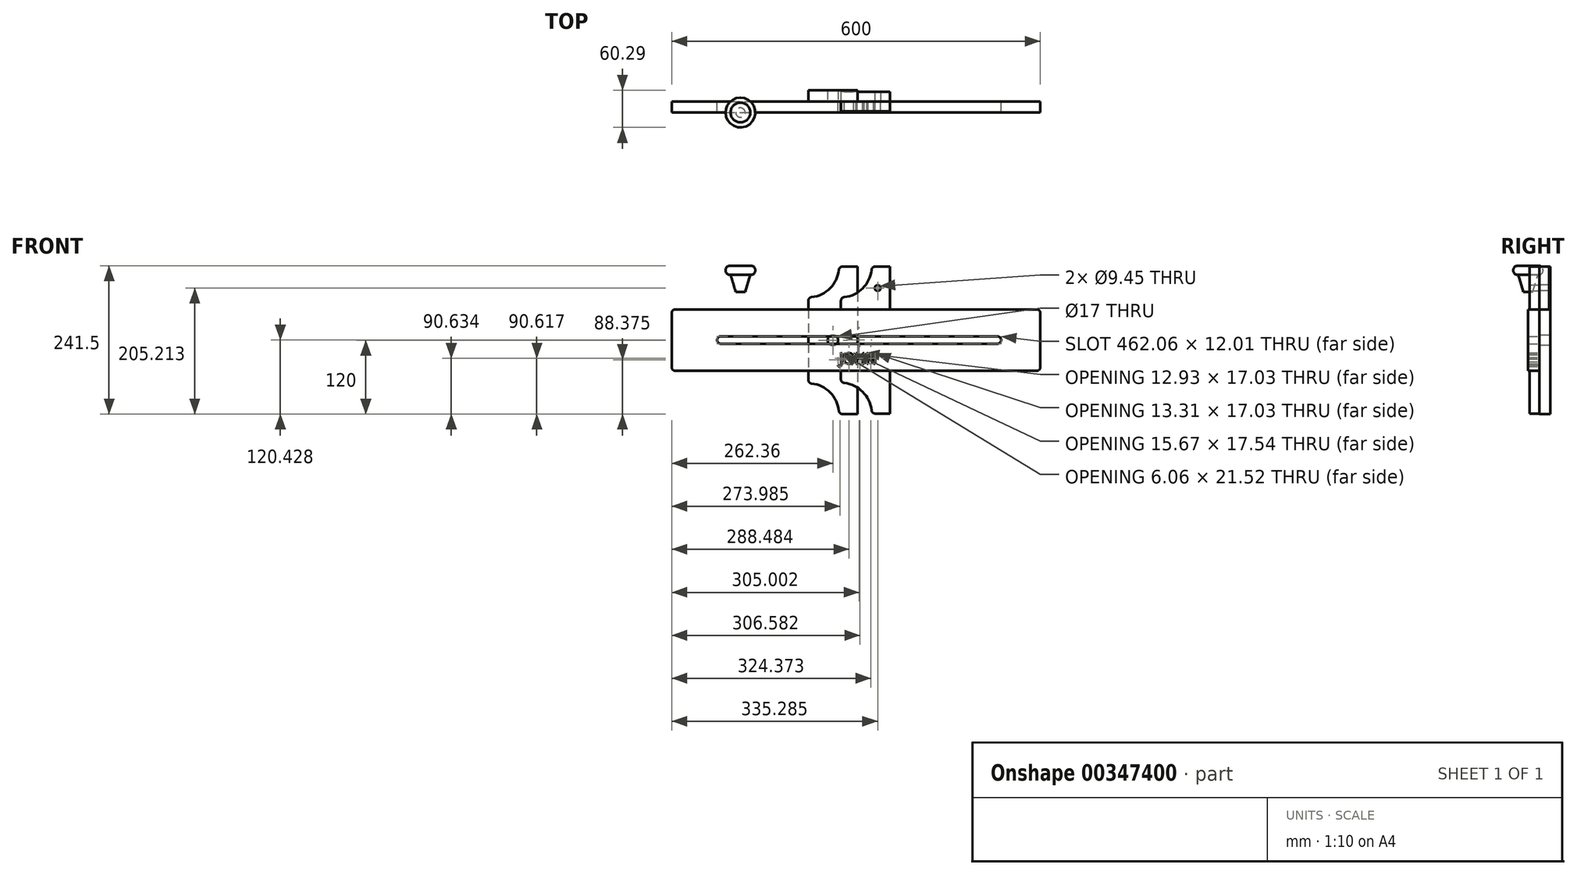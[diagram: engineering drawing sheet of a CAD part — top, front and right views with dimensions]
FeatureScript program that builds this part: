
annotation { "Feature Type Name" : "Feature", "Feature Type Description" : "" }
export const myFeature = defineFeature(function(context is Context, id is Id, definition is map)
    precondition{}
    {
        {
            var Q0;
            Q0=qCreatedBy(makeId("Front.planeOp"),FACE);
            var sketch = newSketch(context, id + "F0", { "sketchPlane" : qUnion([Q0])});
            skLineSegment(sketch, "E0.bottom", {"start": v(-296.36, 50.43) * mm, "end": v(291.64, 50.43) * mm});
            skLineSegment(sketch, "E0.top", {"start": v(-296.36, -49.57) * mm, "end": v(291.64, -49.57) * mm});
            skLineSegment(sketch, "E0.left", {"start": v(-302.36, 44.43) * mm, "end": v(-302.36, -43.57) * mm});
            skLineSegment(sketch, "E0.right", {"start": v(297.64, 44.43) * mm, "end": v(297.64, -43.57) * mm});
            skLineSegment(sketch, "E1", {"start": v(-302.36, 0.43) * mm, "end": v(297.64, 0.43) * mm});
            skCircle(sketch, "E2", {"center": v(-222.39, 0.43) * mm, "radius": 6 * mm});
            skCircle(sketch, "E3", {"center": v(227.67, 0.43) * mm, "radius": 6 * mm});
            skLineSegment(sketch, "E4", {"start": v(-222.39, -5.58) * mm, "end": v(227.67, -5.57) * mm});
            skLineSegment(sketch, "E5", {"start": v(227.67, 6.43) * mm, "end": v(-222.39, 6.43) * mm});
            skPoint(sketch, "E6.visualSharp", {"position": v(-302.36, 50.43) * mm});
            skArc(sketch, "E6.filletArc", {"start": v(-296.36, 50.43) * mm, "mid": v(-300.6, 48.67) * mm, "end": v(-302.36, 44.43) * mm});
            skPoint(sketch, "E7.visualSharp", {"position": v(-302.36, -49.57) * mm});
            skArc(sketch, "E7.filletArc", {"start": v(-302.36, -43.57) * mm, "mid": v(-300.6, -47.81) * mm, "end": v(-296.36, -49.57) * mm});
            skPoint(sketch, "E8.visualSharp", {"position": v(297.64, 50.43) * mm});
            skArc(sketch, "E8.filletArc", {"start": v(297.64, 44.43) * mm, "mid": v(295.88, 48.67) * mm, "end": v(291.64, 50.43) * mm});
            skPoint(sketch, "E9.visualSharp", {"position": v(297.64, -49.57) * mm});
            skArc(sketch, "E9.filletArc", {"start": v(291.64, -49.57) * mm, "mid": v(295.88, -47.81) * mm, "end": v(297.64, -43.57) * mm});
            skText(sketch, "E10", { "text": "JOHN", "fontName": "OpenSans-Regular.ttf"});
            const initialGuessF0  = {"E10": [-0.02954, -0.0379, 1, 0, 0.01718]};
            skSetInitialGuess(sketch, initialGuessF0);
            skSolve(sketch);
        }
        {
            var Q0;
            {var subQ6=sQuery(id+"F0.wireOp",EDGE,"E0.bottom");Q0=makeQuery(id+"F0.imprint","IMPRINT",FACE,{"disambiguationData":[TD([[makeQuery(id+"F0.imprint","IMPRINT",EDGE,{"derivedFrom":subQ6}),-1.0]])]});}
            var Q1;
            {var subQ1=sQuery(id+"F0.wireOp",EDGE,"E0.top");Q1=makeQuery(id+"F0.imprint","IMPRINT",FACE,{"disambiguationData":[TD([[makeQuery(id+"F0.imprint","IMPRINT",EDGE,{"derivedFrom":subQ1}),1.0]])]});}
            var Q2;
            Q2=sQuery(id+"F0.wireOp",EDGE,"E0.bottom");
            var Q3;
            Q3=sQuery(id+"F0.wireOp",EDGE,"E0.left");
            var Q4;
            Q4=sQuery(id+"F0.wireOp",EDGE,"E0.top");
            var Q5;
            Q5=sQuery(id+"F0.wireOp",EDGE,"E0.right");
            extrude(context, id + "F1", {"entities" : qUnion([Q0, Q1]), "surfaceEntities" : qUnion([Q2, Q3, Q4, Q5]), "depth" : 18 * mm});
        }
        {
            var Q0;
            Q0=qCreatedBy(makeId("Front.planeOp"),FACE);
            var sketch = newSketch(context, id + "F2", { "sketchPlane" : qUnion([Q0])});
            skLineSegment(sketch, "E11.left", {"start": v(0, 120) * mm, "end": v(0, 0) * mm});
            skPoint(sketch, "E12.visualSharp", {"position": v(-80, 120) * mm});
            skArc(sketch, "E13.MirrorCS", {"start": v(-30.29, 114.64) * mm, "mid": v(-44.64, 84.64) * mm, "end": v(-74.64, 70.29) * mm});
            skLineSegment(sketch, "E14", {"start": v(-24.32, 120) * mm, "end": v(0, 120) * mm});
            skLineSegment(sketch, "E15", {"start": v(-80, 64.32) * mm, "end": v(-80, 6) * mm});
            skPoint(sketch, "E16.visualSharp", {"position": v(-80, 0) * mm});
            skPoint(sketch, "E17.visualSharp", {"position": v(-80, 70) * mm});
            skArc(sketch, "E17.filletArc", {"start": v(-74.64, 70.29) * mm, "mid": v(-78.46, 68.33) * mm, "end": v(-80, 64.32) * mm});
            skPoint(sketch, "E18.visualSharp", {"position": v(-30, 120) * mm});
            skArc(sketch, "E18.filletArc", {"start": v(-24.32, 120) * mm, "mid": v(-28.33, 118.46) * mm, "end": v(-30.29, 114.64) * mm});
            skLineSegment(sketch, "E19", {"start": v(-80, 6) * mm, "end": v(-80, 0) * mm});
            skLineSegment(sketch, "E20.MirrorCS", {"start": v(0, -120) * mm, "end": v(0, 0) * mm});
            skArc(sketch, "E21.MirrorCS", {"start": v(-74.64, -70.29) * mm, "mid": v(-78.46, -68.33) * mm, "end": v(-80, -64.32) * mm});
            skArc(sketch, "E22.MirrorCS", {"start": v(-24.32, -120) * mm, "mid": v(-28.33, -118.46) * mm, "end": v(-30.29, -114.64) * mm});
            skPoint(sketch, "E23.MirrorP", {"position": v(-30, -120) * mm});
            skPoint(sketch, "E24.MirrorP", {"position": v(-80, -70) * mm});
            skPoint(sketch, "E25.MirrorP", {"position": v(-80, -120) * mm});
            skLineSegment(sketch, "E26.MirrorCS", {"start": v(-24.32, -120) * mm, "end": v(0, -120) * mm});
            skLineSegment(sketch, "E27.MirrorCS", {"start": v(-80, -64.32) * mm, "end": v(-80, -6) * mm});
            skPoint(sketch, "E28.MirrorP", {"position": v(-83.16, 0) * mm});
            skArc(sketch, "E29.MirrorCS", {"start": v(-30.29, -114.64) * mm, "mid": v(-44.64, -84.64) * mm, "end": v(-74.64, -70.29) * mm});
            skLineSegment(sketch, "E30", {"start": v(-80, -6) * mm, "end": v(-80, 0) * mm});
            skCircle(sketch, "E31", {"center": v(-40, 0) * mm, "radius": 8.5 * mm});
            skLineSegment(sketch, "E32", {"start": v(-80, 0) * mm, "end": v(0, 0) * mm});
            skSolve(sketch);
        }
        {
            var Q0;
            Q0 = qSketchRegion(id + "F2", true);
            extrude(context, id + "F3", {"entities" : qUnion([Q0]), "oppositeDirection" : true, "depth" : 18 * mm});
        }
        {
            var Q0;
            Q0=sQuery(id+"F2.wireOp",EDGE,"E31");
            extrude(context, id + "F4", {"bodyType" : ToolBodyType.SURFACE, "surfaceEntities" : qUnion([Q0]), "oppositeDirection" : true, "depth" : 18 * mm});
        }
        {
            var Q0;
            Q0=qCreatedBy(makeId("Front.planeOp"),FACE);
            var sketch = newSketch(context, id + "F5", { "sketchPlane" : qUnion([Q0])});
            skPoint(sketch, "E33.visualSharp", {"position": v(-26.9, 120) * mm});
            skArc(sketch, "E34.MirrorCS", {"start": v(22.8, 114.64) * mm, "mid": v(8.45, 84.64) * mm, "end": v(-21.55, 70.29) * mm});
            skLineSegment(sketch, "E35", {"start": v(28.77, 120) * mm, "end": v(53.1, 120) * mm});
            skPoint(sketch, "E36.visualSharp", {"position": v(-26.91, 0) * mm});
            skPoint(sketch, "E37.visualSharp", {"position": v(-26.9, 70) * mm});
            skArc(sketch, "E37.filletArc", {"start": v(-21.55, 70.29) * mm, "mid": v(-25.37, 68.33) * mm, "end": v(-26.9, 64.32) * mm});
            skPoint(sketch, "E38.visualSharp", {"position": v(23.1, 120) * mm});
            skArc(sketch, "E38.filletArc", {"start": v(28.77, 120) * mm, "mid": v(24.76, 118.46) * mm, "end": v(22.8, 114.64) * mm});
            skPoint(sketch, "E39.MirrorP", {"position": v(-26.9, -70) * mm});
            skPoint(sketch, "E40.MirrorP", {"position": v(-26.9, -120) * mm});
            skPoint(sketch, "E41.MirrorP", {"position": v(-30.07, 0) * mm});
            skLineSegment(sketch, "E42", {"start": v(53.15, 50.43) * mm, "end": v(-26.9, 50.43) * mm});
            skLineSegment(sketch, "E43", {"start": v(-26.9, 64.32) * mm, "end": v(-26.9, 50.43) * mm});
            skLineSegment(sketch, "E44", {"start": v(53.1, 120) * mm, "end": v(53.15, 50.43) * mm});
            skLineSegment(sketch, "E45.MirrorCS", {"start": v(53.15, -49.57) * mm, "end": v(-26.9, -49.57) * mm});
            skLineSegment(sketch, "E46.MirrorCS", {"start": v(-26.9, -63.47) * mm, "end": v(-26.9, -49.57) * mm});
            skArc(sketch, "E47.MirrorCS", {"start": v(-21.55, -69.43) * mm, "mid": v(-25.37, -67.48) * mm, "end": v(-26.9, -63.47) * mm});
            skArc(sketch, "E48.MirrorCS", {"start": v(22.8, -113.79) * mm, "mid": v(8.45, -83.79) * mm, "end": v(-21.55, -69.43) * mm});
            skArc(sketch, "E49.MirrorCS", {"start": v(28.77, -119.14) * mm, "mid": v(24.76, -117.6) * mm, "end": v(22.8, -113.79) * mm});
            skLineSegment(sketch, "E50.MirrorCS", {"start": v(53.1, -119.14) * mm, "end": v(53.15, -49.57) * mm});
            skLineSegment(sketch, "E51.MirrorCS", {"start": v(28.77, -119.14) * mm, "end": v(53.1, -119.14) * mm});
            skCircle(sketch, "E52", {"center": v(32.93, 85.21) * mm, "radius": 4.73 * mm});
            skPoint(sketch, "E52.centerSnap0", {"position": v(53.12, 85.21) * mm});
            skSolve(sketch);
        }
        {
            var Q0;
            Q0 = qSketchRegion(id + "F5", true);
            extrude(context, id + "F6", {"entities" : qUnion([Q0]), "depth" : 16 * mm});
        }
        {
            var Q0;
            Q0=makeQuery(id+"F1.opExtrude","CAP_FACE",FACE,{"disambiguationData":[OSD([sQuery(id+"F0.wireOp",EDGE,"E0.bottom"),sQuery(id+"F0.wireOp",EDGE,"E0.top"),sQuery(id+"F0.wireOp",EDGE,"E0.left"),sQuery(id+"F0.wireOp",EDGE,"E0.right"),sQuery(id+"F0.wireOp",EDGE,"E2"),sQuery(id+"F0.wireOp",EDGE,"E3"),sQuery(id+"F0.wireOp",EDGE,"E4"),sQuery(id+"F0.wireOp",EDGE,"E5"),sQuery(id+"F0.wireOp",EDGE,"E6.filletArc"),sQuery(id+"F0.wireOp",EDGE,"E7.filletArc"),sQuery(id+"F0.wireOp",EDGE,"E8.filletArc"),sQuery(id+"F0.wireOp",EDGE,"E9.filletArc"),sQuery(id+"F0.wireOp",EDGE,"E10.sketch_text.stroke-0"),sQuery(id+"F0.wireOp",EDGE,"E10.sketch_text.stroke-1"),sQuery(id+"F0.wireOp",EDGE,"E10.sketch_text.stroke-2"),sQuery(id+"F0.wireOp",EDGE,"E10.sketch_text.stroke-3"),sQuery(id+"F0.wireOp",EDGE,"E10.sketch_text.stroke-4"),sQuery(id+"F0.wireOp",EDGE,"E10.sketch_text.stroke-5"),sQuery(id+"F0.wireOp",EDGE,"E10.sketch_text.stroke-6"),sQuery(id+"F0.wireOp",EDGE,"E10.sketch_text.stroke-7"),sQuery(id+"F0.wireOp",EDGE,"E10.sketch_text.stroke-8"),sQuery(id+"F0.wireOp",EDGE,"E10.sketch_text.stroke-9"),sQuery(id+"F0.wireOp",EDGE,"E10.sketch_text.stroke-10"),sQuery(id+"F0.wireOp",EDGE,"E10.sketch_text.stroke-11"),sQuery(id+"F0.wireOp",EDGE,"E10.sketch_text.stroke-12"),sQuery(id+"F0.wireOp",EDGE,"E10.sketch_text.stroke-13"),sQuery(id+"F0.wireOp",EDGE,"E10.sketch_text.stroke-14"),sQuery(id+"F0.wireOp",EDGE,"E10.sketch_text.stroke-15"),sQuery(id+"F0.wireOp",EDGE,"E10.sketch_text.stroke-16"),sQuery(id+"F0.wireOp",EDGE,"E10.sketch_text.stroke-17"),sQuery(id+"F0.wireOp",EDGE,"E10.sketch_text.stroke-26"),sQuery(id+"F0.wireOp",EDGE,"E10.sketch_text.stroke-27"),sQuery(id+"F0.wireOp",EDGE,"E10.sketch_text.stroke-28"),sQuery(id+"F0.wireOp",EDGE,"E10.sketch_text.stroke-29"),sQuery(id+"F0.wireOp",EDGE,"E10.sketch_text.stroke-30"),sQuery(id+"F0.wireOp",EDGE,"E10.sketch_text.stroke-31"),sQuery(id+"F0.wireOp",EDGE,"E10.sketch_text.stroke-32"),sQuery(id+"F0.wireOp",EDGE,"E10.sketch_text.stroke-33"),sQuery(id+"F0.wireOp",EDGE,"E10.sketch_text.stroke-34"),sQuery(id+"F0.wireOp",EDGE,"E10.sketch_text.stroke-35"),sQuery(id+"F0.wireOp",EDGE,"E10.sketch_text.stroke-36"),sQuery(id+"F0.wireOp",EDGE,"E10.sketch_text.stroke-37"),sQuery(id+"F0.wireOp",EDGE,"E10.sketch_text.stroke-38"),sQuery(id+"F0.wireOp",EDGE,"E10.sketch_text.stroke-39"),sQuery(id+"F0.wireOp",EDGE,"E10.sketch_text.stroke-40"),sQuery(id+"F0.wireOp",EDGE,"E10.sketch_text.stroke-41"),sQuery(id+"F0.wireOp",EDGE,"E10.sketch_text.stroke-42"),sQuery(id+"F0.wireOp",EDGE,"E10.sketch_text.stroke-43"),sQuery(id+"F0.wireOp",EDGE,"E10.sketch_text.stroke-44"),sQuery(id+"F0.wireOp",EDGE,"E10.sketch_text.stroke-45"),sQuery(id+"F0.wireOp",EDGE,"E10.sketch_text.stroke-46"),sQuery(id+"F0.wireOp",EDGE,"E10.sketch_text.stroke-47"),sQuery(id+"F0.wireOp",EDGE,"E10.sketch_text.stroke-48"),sQuery(id+"F0.wireOp",EDGE,"E10.sketch_text.stroke-49"),sQuery(id+"F0.wireOp",EDGE,"E10.sketch_text.stroke-50"),sQuery(id+"F0.wireOp",EDGE,"E10.sketch_text.stroke-51"),sQuery(id+"F0.wireOp",EDGE,"E10.sketch_text.stroke-52")])],"isStart":false});
            var sketch = newSketch(context, id + "F7", { "sketchPlane" : qUnion([Q0])});
            skLineSegment(sketch, "E53", {"start": v(-190.46, 78.75) * mm, "end": v(-190.46, 106.57) * mm});
            skLineSegment(sketch, "E54", {"start": v(-174.56, 106.57) * mm, "end": v(-182.83, 78.75) * mm});
            skLineSegment(sketch, "E55", {"start": v(-190.46, 106.57) * mm, "end": v(-190.46, 121.47) * mm});
            skLineSegment(sketch, "E56", {"start": v(-190.46, 121.47) * mm, "end": v(-174.34, 121.47) * mm});
            skArc(sketch, "E57", {"start": v(-174.56, 106.57) * mm, "mid": v(-166.17, 113.9) * mm, "end": v(-174.34, 121.47) * mm});
            skLineSegment(sketch, "E58", {"start": v(-190.46, 78.75) * mm, "end": v(-182.83, 78.75) * mm});
            skSolve(sketch);
        }
        {
            var Q0;
            Q0=makeQuery(id+"F7.imprint","IMPRINT",FACE,{"disambiguationData":[TD([[makeQuery(id+"F7.imprint","IMPRINT",EDGE,{"derivedFrom":sQuery(id+"F7.wireOp",EDGE,"E53")}),-1.0]])]});
            var Q1;
            Q1=sQuery(id+"F7.wireOp",EDGE,"E53");
            revolve(context, id + "F8", {"entities" : qUnion([Q0]), "axis" : qUnion([Q1]), "revolveType" : RevolveType.FULL});
        }
        {
            var Q0;
            Q0=makeQuery(id+"F6.opExtrude","SWEPT_BODY",BODY,{"disambiguationData":[OSD([sQuery(id+"F5.wireOp",EDGE,"E34.MirrorCS"),sQuery(id+"F5.wireOp",EDGE,"E35"),sQuery(id+"F5.wireOp",EDGE,"E37.filletArc"),sQuery(id+"F5.wireOp",EDGE,"E38.filletArc"),sQuery(id+"F5.wireOp",EDGE,"E42"),sQuery(id+"F5.wireOp",EDGE,"E43"),sQuery(id+"F5.wireOp",EDGE,"E44"),sQuery(id+"F5.wireOp",EDGE,"E52")])]});
            var Q1;
            Q1=qCreatedBy(makeId("Front.planeOp"),FACE);
            mirror(context, id + "F9", {"entities" : qUnion([Q0]), "mirrorPlane" : qUnion([Q1])});
        }
    });
